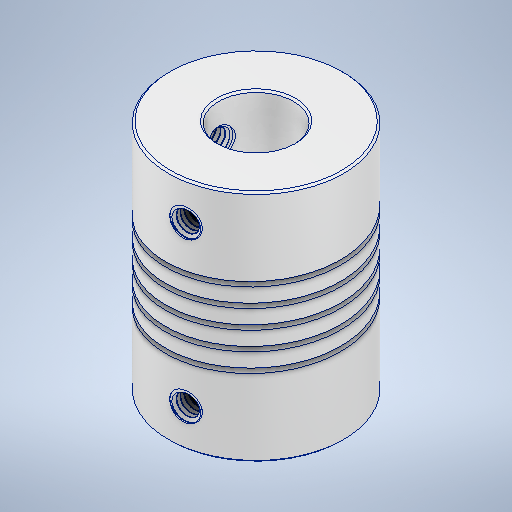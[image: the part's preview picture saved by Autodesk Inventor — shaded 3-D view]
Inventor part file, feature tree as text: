
AUTODESK INVENTOR PART (.ipt)
format: ipt  version: 2025.2 (Build 292293000, 293)  size: 2,700,800 bytes
history: native  units: mm
features: sketch x6, helix x5, thread x4, revolve x4, extrude x2, chamfer x2, hole x1, pattern_circular x1
ambient origin geometry x8: Origin, YZ Plane, XZ Plane, XY Plane, X Axis, Y Axis, Z Axis, Center Point
bodies: Solid1 (feature_tree), Solid2 (feature_tree), Solid3 (feature_tree), Solid4 (feature_tree), Solid5 (feature_tree)
feature tree (25):
  extrude  "Extrusion1"  Depth=25.0mm TaperAngle=0.0deg
  hole  "Hole1"  [1 undecoded]
  extrude  "Extrusion2"  Depth=10.0mm TaperAngle=0.0deg
  chamfer  "Chamfer1"  Distance=20.0mm
  pattern_circular  "Circular Pattern1"  [2 undecoded]
  thread  "Thread1"  [1 undecoded]
  thread  "Thread2"  [1 undecoded]
  thread  "Thread3"  [1 undecoded]
  thread  "Thread4"  [1 undecoded]
  revolve  "Revolution1"  [1 undecoded]
  helix  "Coil1"  [1 undecoded]
  revolve  "Revolution2"  [1 undecoded]
  helix  "Coil2"  [1 undecoded]
  revolve  "Revolution3"  [1 undecoded]
  helix  "Coil3"  [1 undecoded]
  revolve  "Revolution4"  [1 undecoded]
  helix  "Coil4"  [1 undecoded]
  helix  "Coil5"  [1 undecoded]
  chamfer  "Chamfer2"  Distance=9.599311mm
  sketch  "Sketch3"  dims[d0=18.7mm d1=25.0mm d2=0.0mm]
  sketch  "Sketch5"  dims[d3=5.0mm d4=6.0mm d5=8.0mm d6=18.0mm d7=90.0deg d8=7.0mm d9=0.0mm d10=4.0mm]
  sketch  "Sketch7"  dims[d11=3.0mm d12=10.0mm d13=0.0mm d14=20.0mm d15=17.453293mm]
  sketch  "Sketch9"  dims[d18=0.15mm d19=2.0mm d20=45.0deg]
  sketch  "Sketch11"  dims[d21=5.2mm d22=0.0mm]
  sketch  "Sketch12"  dims[d23=5.2mm d24=0.0mm d25=6.7mm d26=0.0mm d27=6.7mm d28=0.0mm d29=9.599311mm d30=0.080042mm d31=0.080042mm d34=0.5mm d36=9.599311mm d38=0.0mm d39=0.5005mm d40=6.2mm d41=10.0mm d42=0.0mm d43=0.0mm d44=0.0mm d45=0.0mm d46=0.0mm d47=9.599311mm d48=0.080042mm d49=0.080042mm d52=0.5mm d54=9.599311mm d56=0.0mm d57=0.5005mm d58=6.2mm d59=10.0mm d60=0.0mm d61=0.0mm d62=0.0mm d63=0.0mm d64=0.0mm d65=9.599311mm d66=0.080042mm d67=0.080042mm d70=0.5mm d72=9.599311mm d74=0.0mm d75=0.5005mm d76=7.7mm d77=10.0mm d78=0.0mm d79=0.0mm d80=0.0mm d81=0.0mm d82=0.0mm d83=9.599311mm d84=0.080042mm d85=0.080042mm d88=0.5mm d90=9.599311mm d92=0.0mm d93=0.5005mm d94=7.7mm d95=10.0mm d96=0.0mm d97=0.0mm d98=0.0mm d99=0.0mm d100=0.0mm d101=0.5mm d102=7.0mm d103=7.0mm d104=2.0mm d105=9.9mm d106=50.0mm d107=0.0mm d108=90.0deg d109=90.0deg d110=0.0mm d111=0.0mm d112=0.2mm d113=2.0mm d114=45.0deg]
note: 16 required parameter values undecoded (feature->parameter linkage not recoverable at this tier; creation-order binding heuristic only, values carry confidence <= 0.55)